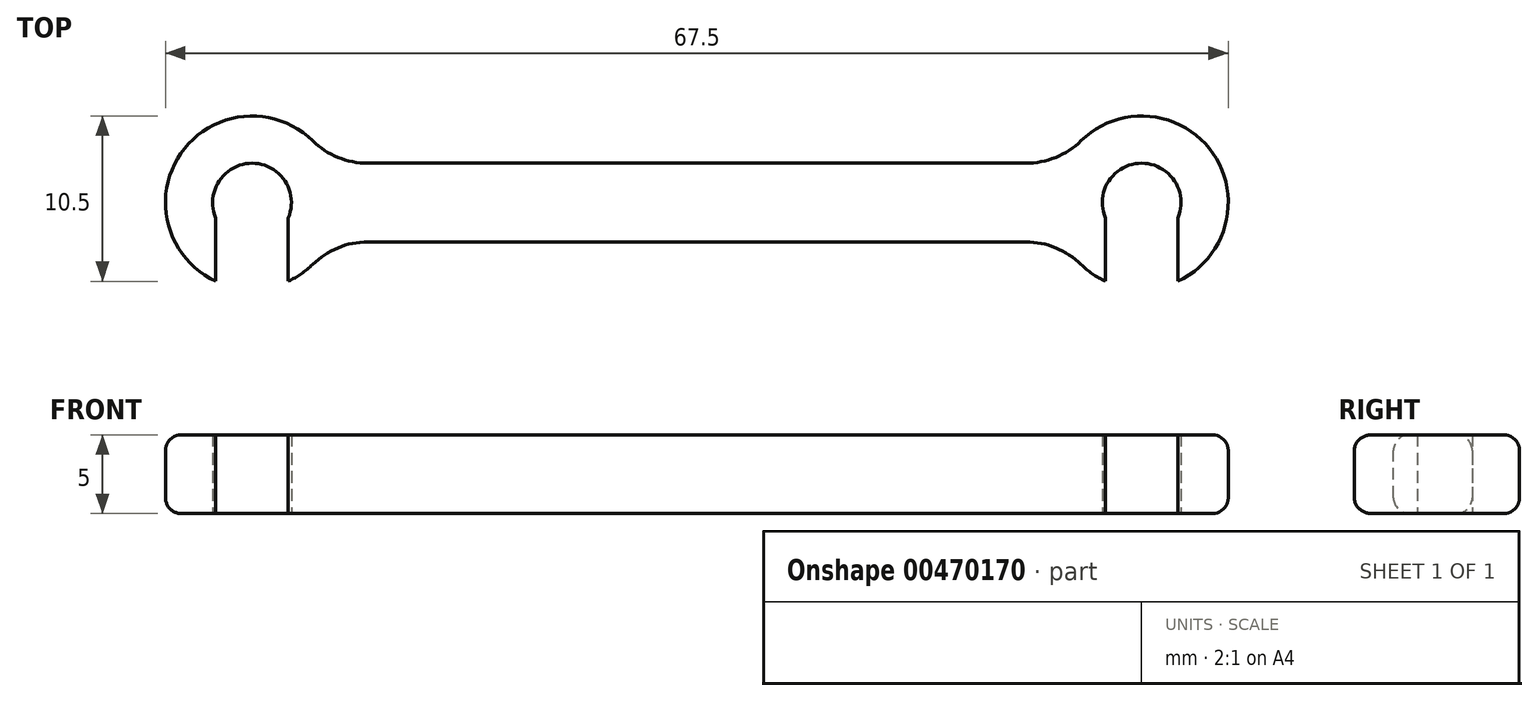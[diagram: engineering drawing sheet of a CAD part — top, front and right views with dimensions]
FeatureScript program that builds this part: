
annotation { "Feature Type Name" : "Feature", "Feature Type Description" : "" }
export const myFeature = defineFeature(function(context is Context, id is Id, definition is map)
    precondition{}
    {
        {
            var Q0;
            Q0=qCreatedBy(makeId("Top.planeOp"),FACE);
            var sketch = newSketch(context, id + "F0", { "sketchPlane" : qUnion([Q0])});
            skLineSegment(sketch, "E0", {"start": v(-28.25, 0) * mm, "end": v(28.25, 0) * mm, "construction": true});
            skCircle(sketch, "E1", {"center": v(-28.25, 0) * mm, "radius": 2.5 * mm});
            skCircle(sketch, "E2", {"center": v(28.25, 0) * mm, "radius": 2.5 * mm});
            skCircle(sketch, "E3", {"center": v(28.25, 0) * mm, "radius": 5.5 * mm});
            skCircle(sketch, "E4", {"center": v(-28.25, 0) * mm, "radius": 5.5 * mm});
            skLineSegment(sketch, "E5", {"start": v(-23.35, 2.5) * mm, "end": v(23.35, 2.5) * mm});
            skLineSegment(sketch, "E6", {"start": v(-23.35, -2.5) * mm, "end": v(23.35, -2.5) * mm});
            skSolve(sketch);
        }
        {
            var Q0;
            Q0 = qSketchRegion(id + "F0", true);
            extrude(context, id + "F1", {"entities" : qUnion([Q0]), "depth" : 5 * mm, "offsetDistance" : 25 * mm});
        }
        {
            var Q0;
            Q0=makeQuery(id+"F1.opExtrude","SWEPT_EDGE",EDGE,{"disambiguationData":[OSD([sQuery(id+"F0.wireOp",EDGE,"E4"),sQuery(id+"F0.wireOp",EDGE,"E6")])]});
            var Q1;
            Q1=makeQuery(id+"F1.opExtrude","SWEPT_EDGE",EDGE,{"disambiguationData":[OSD([sQuery(id+"F0.wireOp",EDGE,"E4"),sQuery(id+"F0.wireOp",EDGE,"E5")])]});
            var Q2;
            Q2=makeQuery(id+"F1.opExtrude","SWEPT_EDGE",EDGE,{"disambiguationData":[OSD([sQuery(id+"F0.wireOp",EDGE,"E3"),sQuery(id+"F0.wireOp",EDGE,"E5")])]});
            var Q3;
            Q3=makeQuery(id+"F1.opExtrude","SWEPT_EDGE",EDGE,{"disambiguationData":[OSD([sQuery(id+"F0.wireOp",EDGE,"E3"),sQuery(id+"F0.wireOp",EDGE,"E6")])]});
            fillet(context, id + "F2", {"entities" : qUnion([Q0, Q1, Q2, Q3]), "tangentPropagation" : true, "radius" : 5 * mm, "defaultsChanged" : false, "vertexSettings" : [], "allowEdgeOverflow" : false});
        }
        {
            var Q0;
            Q0=makeQuery(id+"F1.opExtrude","CAP_EDGE",EDGE,{"disambiguationData":[OSD([sQuery(id+"F0.wireOp",EDGE,"E6")])],"isStart":false});
            var Q1;
            Q1=makeQuery(id+"F1.opExtrude","CAP_EDGE",EDGE,{"disambiguationData":[OSD([sQuery(id+"F0.wireOp",EDGE,"E6")])],"isStart":true});
            fillet(context, id + "F3", {"entities" : qUnion([Q0, Q1]), "tangentPropagation" : true, "radius" : 1 * mm, "defaultsChanged" : false, "vertexSettings" : [], "allowEdgeOverflow" : false});
        }
        {
            var Q0;
            Q0=qCreatedBy(makeId("Top.planeOp"),FACE);
            var sketch = newSketch(context, id + "F4", { "sketchPlane" : qUnion([Q0])});
            skPoint(sketch, "E7.0", {"position": v(-28.25, 0) * mm});
            skPoint(sketch, "E8.0", {"position": v(28.25, 0) * mm});
            skLineSegment(sketch, "E9", {"start": v(-30.55, 0) * mm, "end": v(-30.55, -8.97) * mm});
            skLineSegment(sketch, "E10", {"start": v(-30.55, -8.97) * mm, "end": v(-25.95, -8.97) * mm});
            skLineSegment(sketch, "E11", {"start": v(-25.95, -8.97) * mm, "end": v(-25.95, 0) * mm});
            skLineSegment(sketch, "E12", {"start": v(-25.95, 0) * mm, "end": v(-30.55, 0) * mm});
            skLineSegment(sketch, "E13.MirrorCS", {"start": v(25.95, -8.97) * mm, "end": v(25.95, 0) * mm});
            skLineSegment(sketch, "E14.MirrorCS", {"start": v(30.55, -8.97) * mm, "end": v(25.95, -8.97) * mm});
            skLineSegment(sketch, "E15.MirrorCS", {"start": v(25.95, 0) * mm, "end": v(30.55, 0) * mm});
            skLineSegment(sketch, "E16.MirrorCS", {"start": v(30.55, 0) * mm, "end": v(30.55, -8.97) * mm});
            skSolve(sketch);
        }
        {
            var Q0;
            Q0 = qSketchRegion(id + "F4", true);
            extrude(context, id + "F5", {"entities" : qUnion([Q0]), "operationType" : NewBodyOperationType.REMOVE, "endBound" : BoundingType.THROUGH_ALL, "depth" : 25 * mm, "offsetDistance" : 25 * mm});
        }
    });
